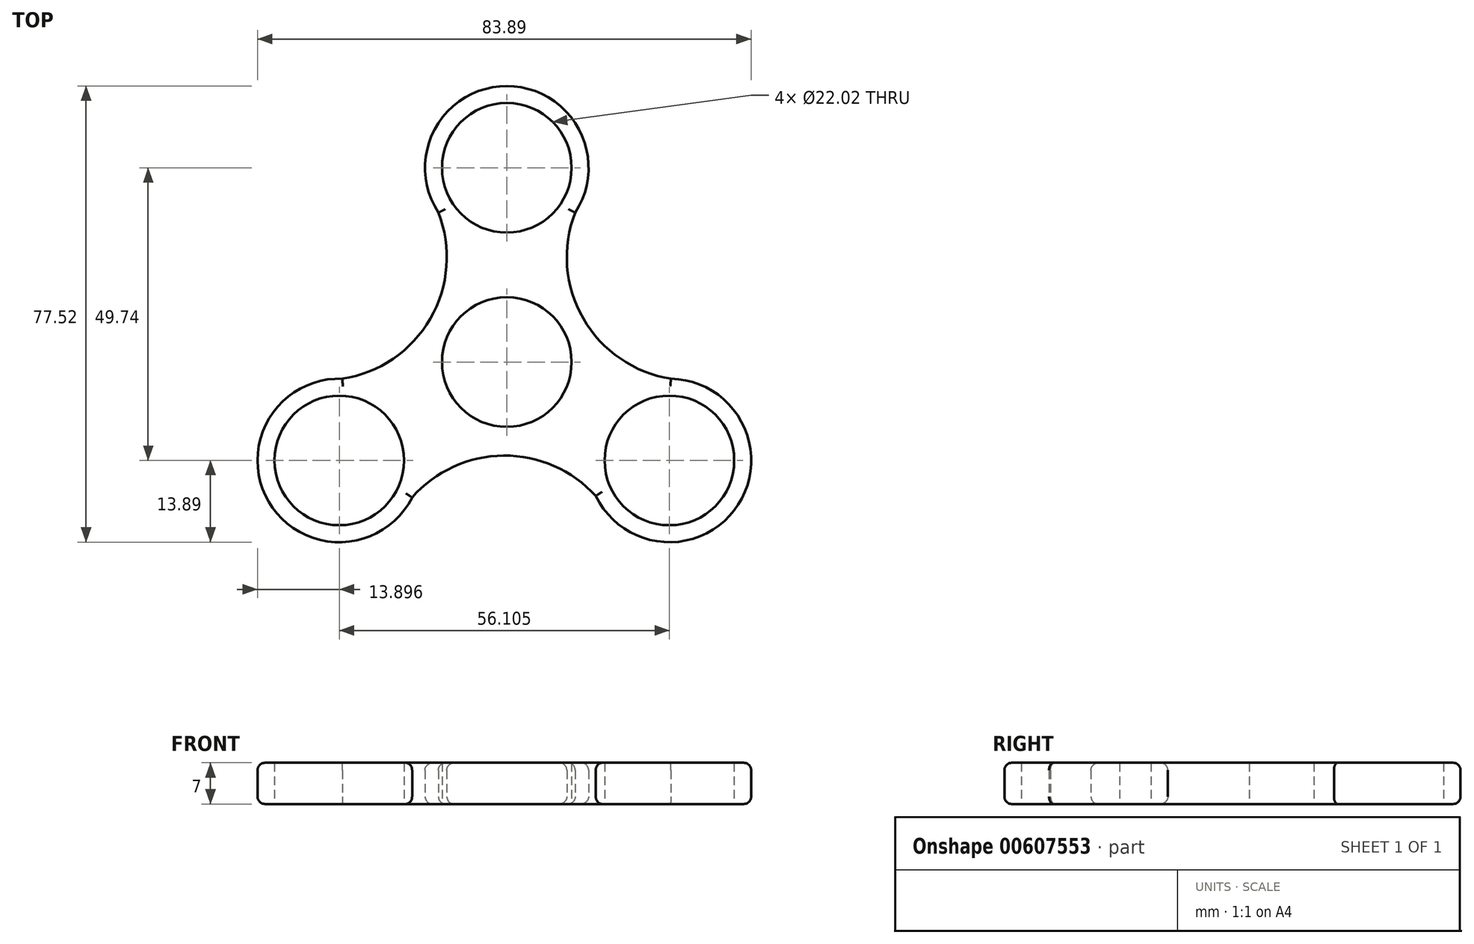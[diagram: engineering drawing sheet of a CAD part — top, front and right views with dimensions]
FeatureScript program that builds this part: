
annotation { "Feature Type Name" : "Feature", "Feature Type Description" : "" }
export const myFeature = defineFeature(function(context is Context, id is Id, definition is map)
    precondition{}
    {
        {
            var Q0;
            Q0=qCreatedBy(makeId("Top.planeOp"),FACE);
            var sketch = newSketch(context, id + "F0", { "sketchPlane" : qUnion([Q0])});
            skCircle(sketch, "E0", {"center": v(0, 0) * mm, "radius": 11.01 * mm});
            skLineSegment(sketch, "E1", {"start": v(0, 0) * mm, "end": v(0, 33.02) * mm, "construction": true});
            skLineSegment(sketch, "E2", {"start": v(0, 0) * mm, "end": v(27.77, -17.86) * mm, "construction": true});
            skCircle(sketch, "E3", {"center": v(-28.47, -16.72) * mm, "radius": 11.01 * mm});
            skCircle(sketch, "E4", {"center": v(0, 33.02) * mm, "radius": 11.01 * mm});
            skLineSegment(sketch, "E5", {"start": v(0, 0) * mm, "end": v(-28.47, -16.72) * mm, "construction": true});
            skCircle(sketch, "E6", {"center": v(-28.47, -16.72) * mm, "radius": 13.9 * mm});
            skCircle(sketch, "E7", {"center": v(0, 33.02) * mm, "radius": 13.9 * mm});
            skArc(sketch, "E8", {"start": v(-27.94, -2.84) * mm, "mid": v(-13, 7.37) * mm, "end": v(-11.62, 25.4) * mm});
            skArc(sketch, "E9.MirrorCS", {"start": v(27.94, -2.84) * mm, "mid": v(13, 7.37) * mm, "end": v(11.62, 25.4) * mm});
            skLineSegment(sketch, "E10", {"start": v(-27.94, -2.84) * mm, "end": v(-27.94, -41.12) * mm, "construction": true});
            skCircle(sketch, "E11", {"center": v(27.63, -16.72) * mm, "radius": 11.01 * mm});
            skCircle(sketch, "E12", {"center": v(27.63, -16.72) * mm, "radius": 13.9 * mm});
            skLineSegment(sketch, "E13", {"start": v(27.94, -2.84) * mm, "end": v(27.94, -36.2) * mm, "construction": true});
            skLineSegment(sketch, "E14", {"start": v(27.94, -2.84) * mm, "end": v(7.74, -34.23) * mm, "construction": true});
            skLineSegment(sketch, "E15", {"start": v(-27.94, -2.84) * mm, "end": v(-8.6, -35.77) * mm, "construction": true});
            skArc(sketch, "E16", {"start": v(15.12, -22.77) * mm, "mid": v(-0.54, -15.9) * mm, "end": v(-16.09, -23.02) * mm});
            skSolve(sketch);
        }
        {
            var Q0;
            Q0=qSketchRegion(id+"F0",true);
            extrude(context, id + "F1", {"entities" : qUnion([Q0]), "depth" : 7 * mm, "offsetDistance" : 25.4 * mm});
        }
        {
            var Q0;
            Q0=makeQuery(id+"F1.opExtrude","CAP_EDGE",EDGE,{"disambiguationData":[OSD([sQuery(id+"F0.wireOp",EDGE,"E8")])],"isStart":false});
            var Q1;
            Q1=makeQuery(id+"F1.opExtrude","CAP_EDGE",EDGE,{"disambiguationData":[OSD([sQuery(id+"F0.wireOp",EDGE,"E16")])],"isStart":false});
            var Q2;
            Q2=makeQuery(id+"F1.opExtrude","CAP_EDGE",EDGE,{"disambiguationData":[OSD([sQuery(id+"F0.wireOp",EDGE,"E9.MirrorCS")])],"isStart":false});
            var Q3;
            Q3=makeQuery(id+"F1.opExtrude","CAP_EDGE",EDGE,{"disambiguationData":[OSD([sQuery(id+"F0.wireOp",EDGE,"E16")])],"isStart":true});
            var Q4;
            Q4=makeQuery(id+"F1.opExtrude","CAP_EDGE",EDGE,{"disambiguationData":[OSD([sQuery(id+"F0.wireOp",EDGE,"E8")])],"isStart":true});
            var Q5;
            Q5=makeQuery(id+"F1.opExtrude","CAP_EDGE",EDGE,{"disambiguationData":[OSD([sQuery(id+"F0.wireOp",EDGE,"E9.MirrorCS")])],"isStart":true});
            var Q6;
            Q6=makeQuery(id+"F1.opExtrude","CAP_EDGE",EDGE,{"disambiguationData":[OSD([sQuery(id+"F0.wireOp",EDGE,"E6")])],"isStart":true});
            var Q7;
            Q7=makeQuery(id+"F1.opExtrude","CAP_EDGE",EDGE,{"disambiguationData":[OSD([sQuery(id+"F0.wireOp",EDGE,"E12")])],"isStart":true});
            var Q8;
            Q8=makeQuery(id+"F1.opExtrude","CAP_EDGE",EDGE,{"disambiguationData":[OSD([sQuery(id+"F0.wireOp",EDGE,"E7")])],"isStart":true});
            var Q9;
            Q9=makeQuery(id+"F1.opExtrude","CAP_EDGE",EDGE,{"disambiguationData":[OSD([sQuery(id+"F0.wireOp",EDGE,"E7")])],"isStart":false});
            var Q10;
            Q10=makeQuery(id+"F1.opExtrude","CAP_EDGE",EDGE,{"disambiguationData":[OSD([sQuery(id+"F0.wireOp",EDGE,"E12")])],"isStart":false});
            var Q11;
            Q11=makeQuery(id+"F1.opExtrude","CAP_EDGE",EDGE,{"disambiguationData":[OSD([sQuery(id+"F0.wireOp",EDGE,"E6")])],"isStart":false});
            fillet(context, id + "F2", {"entities" : qUnion([Q0, Q1, Q2, Q3, Q4, Q5, Q6, Q7, Q8, Q9, Q10, Q11]), "radius" : 1.27 * mm, "tangentPropagation" : true, "allowEdgeOverflow" : false});
        }
    });
